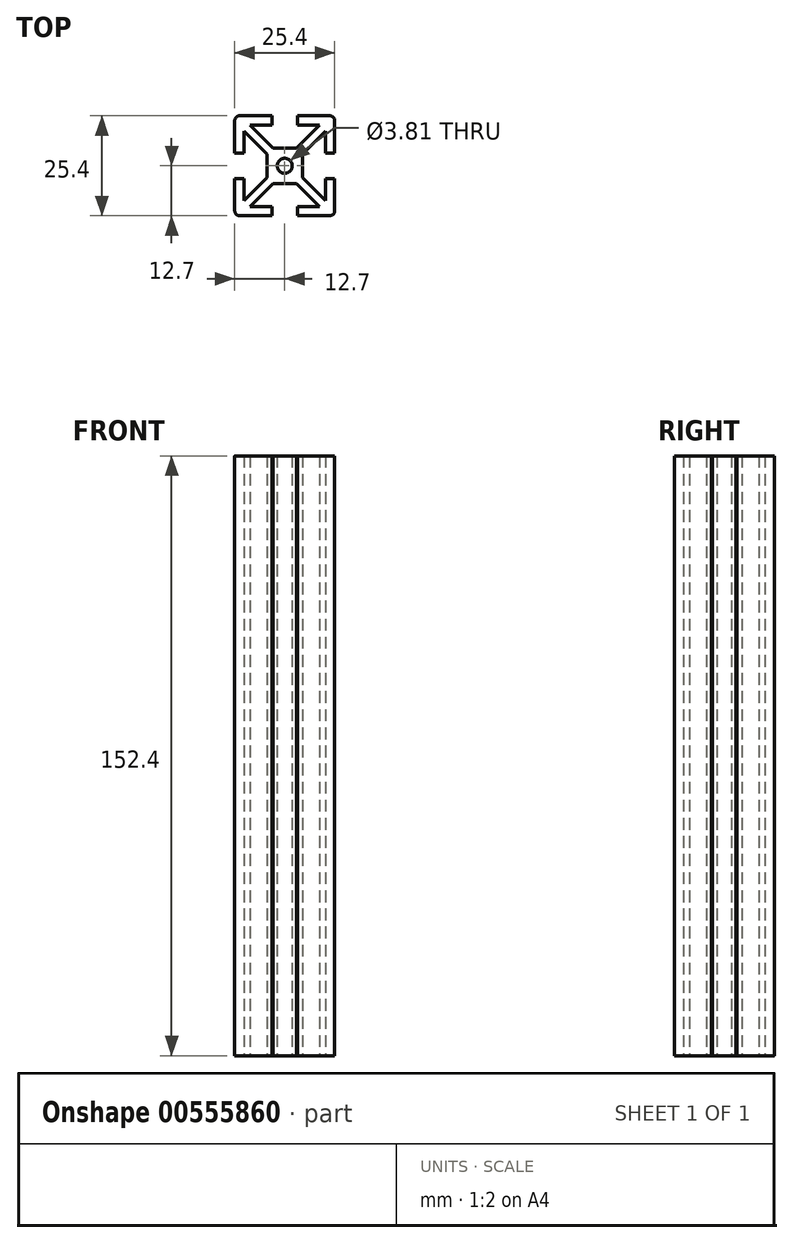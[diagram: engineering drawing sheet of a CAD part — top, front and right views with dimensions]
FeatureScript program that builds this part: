
annotation { "Feature Type Name" : "Feature", "Feature Type Description" : "" }
export const myFeature = defineFeature(function(context is Context, id is Id, definition is map)
    precondition{}
    {
        {
            var Q0;
            Q0=qCreatedBy(makeId("Top.planeOp"),FACE);
            var sketch = newSketch(context, id + "F0", { "sketchPlane" : qUnion([Q0])});
            skLineSegment(sketch, "E0.bottom", {"start": v(-12.7, -12.7) * mm, "end": v(-3.25, -12.7) * mm});
            skLineSegment(sketch, "E0.top", {"start": v(-12.7, 12.7) * mm, "end": v(-3.25, 12.7) * mm});
            skLineSegment(sketch, "E0.left", {"start": v(-12.7, -12.7) * mm, "end": v(-12.7, -3.25) * mm});
            skLineSegment(sketch, "E0.right", {"start": v(12.7, -12.7) * mm, "end": v(12.7, -3.25) * mm});
            skPoint(sketch, "E0.middle", {"position": v(0, 0) * mm});
            skLineSegment(sketch, "E1.bottom", {"start": v(-2.96, -4.52) * mm, "end": v(2.96, -4.52) * mm});
            skLineSegment(sketch, "E1.top", {"start": v(-2.96, 4.52) * mm, "end": v(2.96, 4.52) * mm});
            skLineSegment(sketch, "E1.left", {"start": v(-4.52, -2.96) * mm, "end": v(-4.52, 2.96) * mm});
            skLineSegment(sketch, "E1.right", {"start": v(4.52, -2.96) * mm, "end": v(4.52, 2.96) * mm});
            skLineSegment(sketch, "E2", {"start": v(-12.7, 12.7) * mm, "end": v(12.7, -12.7) * mm, "construction": true});
            skLineSegment(sketch, "E3", {"start": v(12.7, 12.7) * mm, "end": v(-12.7, -12.7) * mm, "construction": true});
            skLineSegment(sketch, "E4.0", {"start": v(-10.36, 8.8) * mm, "end": v(-4.52, 2.96) * mm});
            skLineSegment(sketch, "E5.0", {"start": v(-8.8, 10.36) * mm, "end": v(-2.96, 4.52) * mm});
            skLineSegment(sketch, "E6.0", {"start": v(8.8, 10.36) * mm, "end": v(2.96, 4.52) * mm});
            skLineSegment(sketch, "E7.0", {"start": v(10.36, 8.8) * mm, "end": v(4.52, 2.96) * mm});
            skPoint(sketch, "E8.orphan", {"position": v(-4.52, 4.52) * mm});
            skLineSegment(sketch, "E9.trimOffspring", {"start": v(-4.52, -2.96) * mm, "end": v(-10.36, -8.8) * mm});
            skPoint(sketch, "E10.orphan", {"position": v(4.52, 4.52) * mm});
            skLineSegment(sketch, "E11.trimOffspring", {"start": v(4.52, -2.96) * mm, "end": v(10.36, -8.8) * mm});
            skLineSegment(sketch, "E12.trimOffspring", {"start": v(2.96, -4.52) * mm, "end": v(8.8, -10.36) * mm});
            skPoint(sketch, "E13.orphan", {"position": v(-4.52, -4.52) * mm});
            skPoint(sketch, "E14.orphan", {"position": v(4.52, -4.52) * mm});
            skLineSegment(sketch, "E15", {"start": v(-8.8, -10.36) * mm, "end": v(-3.25, -10.36) * mm});
            skLineSegment(sketch, "E16", {"start": v(10.36, -8.8) * mm, "end": v(10.36, -3.25) * mm});
            skLineSegment(sketch, "E17", {"start": v(8.8, 10.36) * mm, "end": v(3.25, 10.36) * mm});
            skLineSegment(sketch, "E18", {"start": v(-10.36, 8.8) * mm, "end": v(-10.36, 3.25) * mm});
            skLineSegment(sketch, "E19", {"start": v(-8.8, -10.36) * mm, "end": v(-2.96, -4.52) * mm});
            skLineSegment(sketch, "E20", {"start": v(-3.25, -12.7) * mm, "end": v(-3.25, -10.36) * mm});
            skLineSegment(sketch, "E21", {"start": v(3.25, -10.36) * mm, "end": v(3.25, -12.7) * mm});
            skLineSegment(sketch, "E22.trimOffspring", {"start": v(3.25, -10.36) * mm, "end": v(8.8, -10.36) * mm});
            skLineSegment(sketch, "E23.trimOffspring", {"start": v(3.25, -12.7) * mm, "end": v(12.7, -12.7) * mm});
            skLineSegment(sketch, "E24", {"start": v(12.7, -3.25) * mm, "end": v(10.36, -3.25) * mm});
            skLineSegment(sketch, "E25", {"start": v(12.7, 3.25) * mm, "end": v(10.36, 3.25) * mm});
            skLineSegment(sketch, "E26", {"start": v(-12.7, -3.25) * mm, "end": v(-10.36, -3.25) * mm});
            skLineSegment(sketch, "E27", {"start": v(-12.7, 3.25) * mm, "end": v(-10.36, 3.25) * mm});
            skLineSegment(sketch, "E28", {"start": v(-3.25, 12.7) * mm, "end": v(-3.25, 10.36) * mm});
            skLineSegment(sketch, "E29", {"start": v(3.25, 12.7) * mm, "end": v(3.25, 10.36) * mm});
            skLineSegment(sketch, "E30.trimOffspring", {"start": v(10.36, 3.25) * mm, "end": v(10.36, 8.8) * mm});
            skLineSegment(sketch, "E31.trimOffspring", {"start": v(12.7, 3.25) * mm, "end": v(12.7, 12.7) * mm});
            skLineSegment(sketch, "E32.trimOffspring", {"start": v(-3.25, 10.36) * mm, "end": v(-8.8, 10.36) * mm});
            skLineSegment(sketch, "E33.trimOffspring", {"start": v(3.25, 12.7) * mm, "end": v(12.7, 12.7) * mm});
            skLineSegment(sketch, "E34.trimOffspring", {"start": v(-10.36, -3.25) * mm, "end": v(-10.36, -8.8) * mm});
            skLineSegment(sketch, "E35.trimOffspring", {"start": v(-12.7, 3.25) * mm, "end": v(-12.7, 12.7) * mm});
            skCircle(sketch, "E36", {"center": v(0, 0) * mm, "radius": 1.9 * mm});
            skSolve(sketch);
        }
        {
            var Q0;
            Q0=makeQuery(id+"F0.imprint","IMPRINT",FACE,{"disambiguationData":[TD([[makeQuery(id+"F0.imprint","IMPRINT",EDGE,{"derivedFrom":sQuery(id+"F0.wireOp",EDGE,"E0.bottom")}),1.0]])]});
            extrude(context, id + "F1", {"entities" : qUnion([Q0]), "depth" : 152.4 * mm, "offsetDistance" : 25.4 * mm});
        }
        {
            var Q0;
            Q0=makeQuery(id+"F1.opExtrude","SWEPT_EDGE",EDGE,{"disambiguationData":[OSD([sQuery(id+"F0.wireOp",EDGE,"E0.top"),sQuery(id+"F0.wireOp",EDGE,"E35.trimOffspring")])]});
            var Q1;
            Q1=makeQuery(id+"F1.opExtrude","SWEPT_EDGE",EDGE,{"disambiguationData":[OSD([sQuery(id+"F0.wireOp",EDGE,"E31.trimOffspring"),sQuery(id+"F0.wireOp",EDGE,"E33.trimOffspring")])]});
            var Q2;
            Q2=makeQuery(id+"F1.opExtrude","SWEPT_EDGE",EDGE,{"disambiguationData":[OSD([sQuery(id+"F0.wireOp",EDGE,"E0.right"),sQuery(id+"F0.wireOp",EDGE,"E23.trimOffspring")])]});
            var Q3;
            Q3=makeQuery(id+"F1.opExtrude","SWEPT_EDGE",EDGE,{"disambiguationData":[OSD([sQuery(id+"F0.wireOp",EDGE,"E0.bottom"),sQuery(id+"F0.wireOp",EDGE,"E0.left")])]});
            fillet(context, id + "F2", {"entities" : qUnion([Q0, Q1, Q2, Q3]), "radius" : 1.27 * mm, "tangentPropagation" : true, "allowEdgeOverflow" : false});
        }
    });
